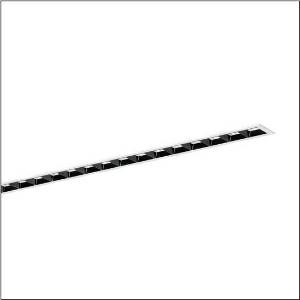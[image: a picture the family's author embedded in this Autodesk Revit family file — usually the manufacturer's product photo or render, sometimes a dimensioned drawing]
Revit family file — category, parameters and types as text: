
# Revit family: silica_r__21_51mx11dc4awb_441a
name_source: partatom
category: Lighting Fixtures
units: mm (PartAtom-declared; Revit-internal decimal feet)

## family parameters
Cut with Voids When Loaded = No
Host = Face
Light Source = No
Part Type = Normal
Room Calculation Point = No
Round Connector Dimension = Use Diameter
Shared = No

## types (1)
- --- (1 x LED, 10800 lm, 64.8 W, 4000K)
    Apparent Load = 65 VA
    CIE Flux Codes = 87 99 100 100 100
    Color Rendering = 80
    Color Temperature = 4000K
    Default Elevation = 1800 mm
    Description = Silica® 21, office luminaire, primary light control with darklight reflector, of PMMA, black, CAT 2 (L<= 3000cd/m²), light emission: direct distribution, primary light characteristic: symmetric, installation type: recessed, LED, rated luminous flux: 10.800lm, luminous efficacy: 167lm/W, light colour: 840, colour temperature: 4000K, with terminal, 3+2-pole, max. 2.5mm², mains connection: 220..240V, AC, 50/60Hz, rated input power: 64.8W, luminaire housing, of aluminium, traffic white (RAL 9016), length: 3.028mm, width: 79mm, height: 53mm, protection rating (complete): IP20, insulation class (complete): insulation class I (protective earthing), certification: CE, permissible operating ambient temperature: 0..+35°C, standard: EN 50419, packaging unit: 1 piece
    Height = 0 mm  [stored 0 ft]
    Lamp = 1 x LED
    Lamp Light Flux = 10800 lm
    Lamp Power = 64.8 W
    Lamp count = 1
    Length = 3027 mm
    Luminous efficacy = 167 lm/W
    Manufacturer = Siteco
    ModVariant = No
    Model = 51MX11DC4AWB
    Mounting Place = Ceiling
    Mounting Type = Recessed
    Number of Poles = 1
    OnlyDefault = Yes
    Power Factor = 1
    Product Name = Silica® 21
    Product group = office luminaire | ceiling recessed
    ProductGroupID = 400
    Protection Class = Protection class I
    Protection Degree = IP 20
    RLX_Detail_Level = 1
    RlxData = <blob elided: 63077 chars, md5=46d44d95>
    Socket = socket
    Standby Power = 0 W
    System Light Flux = 10800 lm
    System Power = 65 W
    Type Comments = factory setting: luminous flux: 100 % | dim-lin: 254 | 367 mA
    Type Image = l_1251632.jpg
    URL = http://relux.com
    VarID = @adj_032555
    Voltage = 0 V
    Weight = 0.00 kg
    Width = 79 mm

note: [stored X ft] marks values corroborated as IEEE doubles in the binary element streams (Revit-internal decimal feet)

## geometry (parser evidence)
native form markers: Blend x4, Sweep x12
no freeform markers — native parametric forms only
